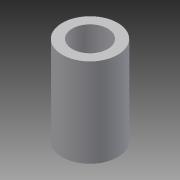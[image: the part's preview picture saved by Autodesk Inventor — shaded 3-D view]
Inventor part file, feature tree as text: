
AUTODESK INVENTOR PART (.ipt)
format: ipt  version: 2013 (Build 170138000, 138)  size: 74,240 bytes
history: native  units: mm
features: extrude x2, sketch x2
ambient origin geometry x8: Origin, YZ Plane, XZ Plane, XY Plane, X Axis, Y Axis, Z Axis, Center Point
bodies: Volumenkörper1 (feature_tree)
feature tree (4):
  extrude  "Extrusion1"  Depth=8.0mm TaperAngle=0.0deg
  extrude  "Extrusion2"  Depth=8.0mm TaperAngle=0.0deg
  sketch  "Skizze1"  dims[d0=5.0mm d2=8.0mm d3=0.0mm]
  sketch  "Skizze3"  dims[d4=3.2mm d6=8.0mm d7=0.0mm d5=1.0mm]
